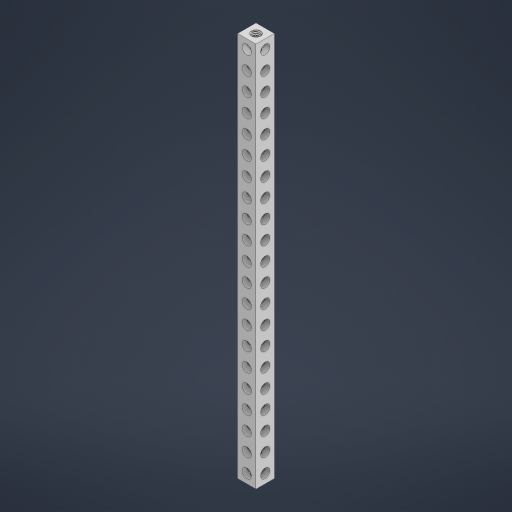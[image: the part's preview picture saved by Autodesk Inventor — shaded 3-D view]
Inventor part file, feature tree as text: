
AUTODESK INVENTOR PART (.ipt)
format: ipt  version: 2023 (Build 270158000, 158)  size: 1,275,904 bytes
history: native  units: in
note: dims shown in document units (in); Inventor stores cm internally (conversion verified against a paired STEP export)
features: mirror x1
ambient origin geometry x8: Origin, YZ Plane, XZ Plane, XY Plane, X Axis, Y Axis, Z Axis, Center Point
bodies: Solid1 (feature_tree)
feature tree (1):
  mirror  "Mirror3"
